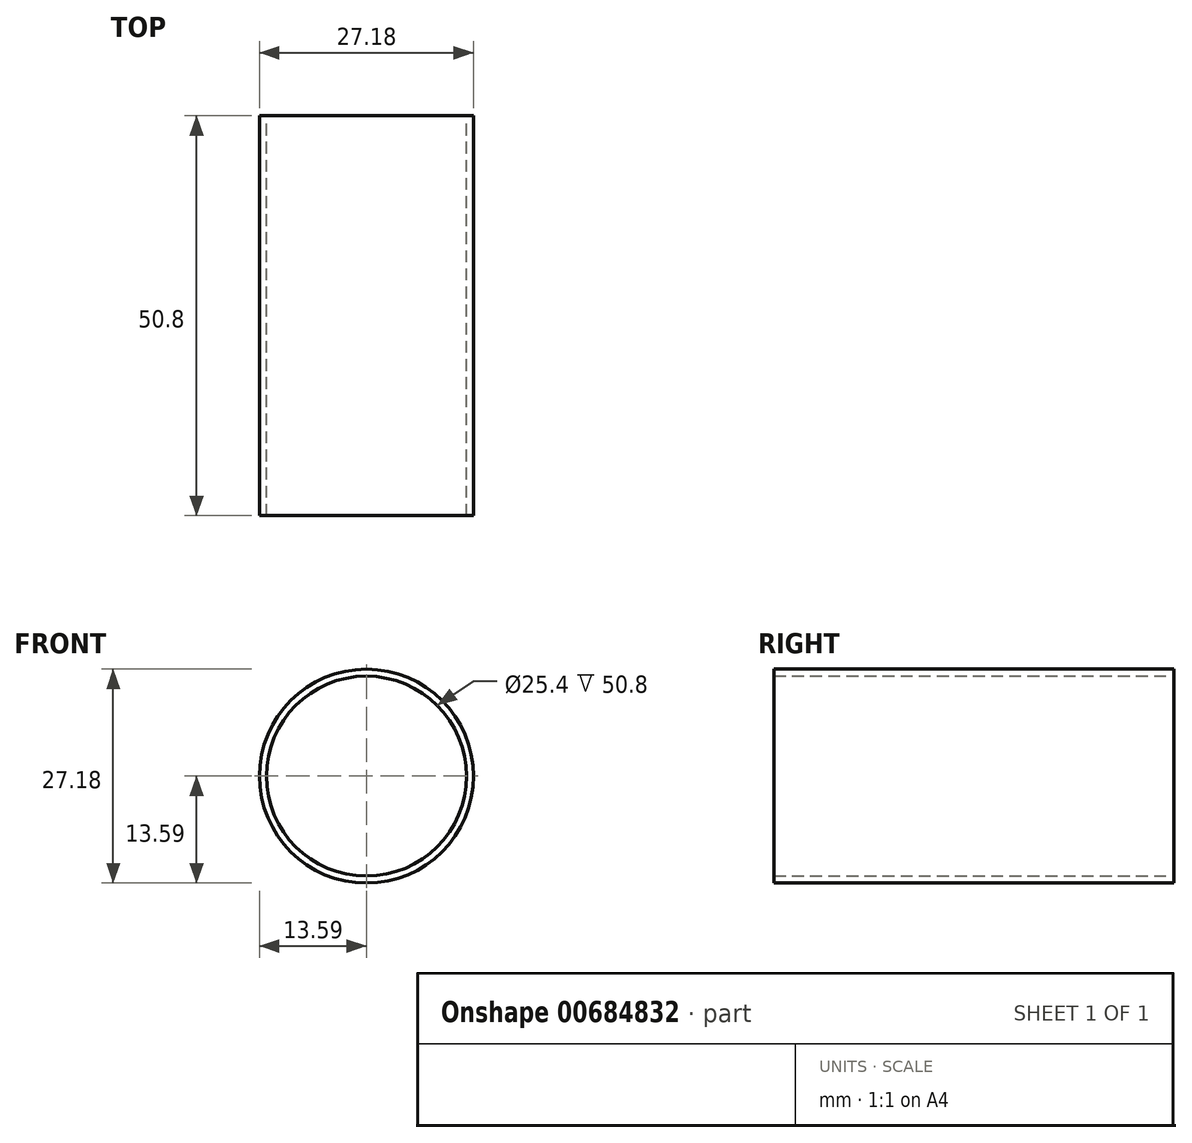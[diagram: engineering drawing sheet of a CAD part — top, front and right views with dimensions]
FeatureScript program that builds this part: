
annotation { "Feature Type Name" : "Feature", "Feature Type Description" : "" }
export const myFeature = defineFeature(function(context is Context, id is Id, definition is map)
    precondition{}
    {
        {
            var Q0;
            Q0=qCreatedBy(makeId("Front.planeOp"),FACE);
            var sketch = newSketch(context, id + "F0", { "sketchPlane" : qUnion([Q0])});
            skCircle(sketch, "E0", {"center": v(0, 0) * mm, "radius": 12.7 * mm});
            skCircle(sketch, "E1", {"center": v(0, 0) * mm, "radius": 13.59 * mm});
            skSolve(sketch);
        }
        {
            var Q0;
            Q0 = qSketchRegion(id + "F0", true);
            extrude(context, id + "F1", {"entities" : qUnion([Q0]), "depth" : 50.8 * mm, "offsetDistance" : 25.4 * mm});
        }
    });
